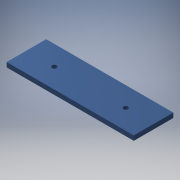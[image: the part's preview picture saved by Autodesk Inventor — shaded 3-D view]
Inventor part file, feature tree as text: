
AUTODESK INVENTOR PART (.ipt)
format: ipt  version: 2016 (Build 200138000, 138)  size: 95,232 bytes
history: native  units: mm
features: reference x2, extrude x1, sketch x1
ambient origin geometry x8: Origin, YZ Plane, XZ Plane, XY Plane, X Axis, Y Axis, Z Axis, Center Point
bodies: Solid1 (feature_tree)
feature tree (4):
  extrude  "Extrusion1"  [1 undecoded]
  sketch  "Sketch1"  dims[d0=3.0mm d1=0.0mm]
  reference  "Reference3"
  reference  "Reference4"
note: 1 required parameter value undecoded (feature->parameter linkage not recoverable at this tier; creation-order binding heuristic only, values carry confidence <= 0.55)
